# Revit family: CENTUM Festpunkt Typ A mit Massivanschluss XL100, Ø60,3 bis Ø139,7 Gummi_
name_source: partatom
category: HLS-Bauteile
revit_build: Autodesk Revit 2018 (Build: 20190510_1515(x64)
units: mm (PartAtom-declared; Revit-internal decimal feet)

## family parameters
Arbeitsebenenbasiert = Ja
Beim Laden mit Abzugskörper schneiden = Nein
Bemaßung runder Anschluss = Durchmesser verwenden
Gemeinsam genutzt = Ja
Immer vertikal = Nein
Klassifizierung = Keine
Raumberechnungspunkt = Nein
Teiletyp = Normal

## types (5) — shared parameters
Anzahl Rohrschellen = 2
Aufbaumaß = 69 mm
Breite Material Rohrschelle = 50 mm
Fabrikat = MEFA
Klammergröße = 2
Kurztext1 = Festpunkt Typ A
Länge Druckstück = 116 mm
Material Druckstücke = Stahl
Materialname Druckstücke = S235JR
Mengeneinheit = St
Oberfläche Druckstücke = blank
Oberfläche Träger + Schellen = galvanisch verzinkt
Rohrschellentyp = Titan HD
Schalldämmeinlage = Gummi TPE/EPDM
Stärke Material Rohrschelle = 5 mm
Vorgabe-Ansicht = 1219 mm
max. Axiale Reaktionskraft = 20 kN
max. Temperaturbeständigkeit = 100 °C
vpe = 1
zero-valued in all types: max. Höhe, max. Rohraußendurchmesser, min. Rohraußendurchmesser

## per-type parameters (varying)
| type | Artikelnummer | Breite | Breite Profilstahl | EAN | Festpunkt | Gewicht | Gewicht pro Bauteil | Höhe Profilstahl | Kurztext2 | Länge Profilstahl | Profilstahltyp | Rohraußendurchmesser |
| CENTUM Festpunkt Typ A, Ø60,3 mm m. XL100 Massivanshluss, Gummi | 9993633 | 148 mm  [stored 0.485564 ft] | 65 mm | 4250928454188 | Festpunkt Typ A m.XL100 Massivanschluss Ø60 bis 114_1 : CENTUM Festpunkt Typ A, Ø 60,3, m. XL100 Massivanschluss, Gummi | 6.12 kg | 6.12 kg | 42 mm | 60,3 mm Gummi | 200 mm  [stored 0.656168 ft] | U65 | 60 mm  [stored 0.19685 ft] |
| CENTUM Festpunkt Typ A, Ø76,1 mm m. XL100 Massivanshluss, Gummi | 9993732 | 166 mm  [stored 0.544619 ft] | 65 mm | 4250928454218 | Festpunkt Typ A m.XL100 Massivanschluss Ø60 bis 114_1 : CENTUM Festpunkt Typ A, Ø 76,1, m. XL100 Massivanschluss, Gummi | 6.36 kg | 6.36 kg | 42 mm | 76,1 mm Gummi | 200 mm  [stored 0.656168 ft] | U65 | 76 mm  [stored 0.249344 ft] |
| CENTUM Festpunkt Typ A, Ø88,9 mm m. XL100 Massivanshluss, Gummi | 9994027 | 179 mm  [stored 0.58727 ft] | 65 mm | 4250928454232 | Festpunkt Typ A m.XL100 Massivanschluss Ø60 bis 114_1 : CENTUM Festpunkt Typ A, Ø 88,9, m. XL100 Massivanschluss, Gummi | 6.55 kg | 6.55 kg | 42 mm | 88,9 mm Gummi | 0 mm  [stored 0 ft] | U65 | 89 mm |
| CENTUM Festpunkt Typ A, Ø114,3 mm m. XL100 Massivanshluss, Gummi | 9993256 | 205 mm  [stored 0.672572 ft] | 65 mm | 4250928454195 | Festpunkt Typ A m.XL100 Massivanschluss Ø60 bis 114_1 : CENTUM Festpunkt Typ A, Ø114,3, m. XL100 Massivanschluss, Gummi | 6.93 kg | 6.93 kg | 42 mm | 114,3 mm Gummi | 200 mm  [stored 0.656168 ft] | U65 | 114 mm  [stored 0.374016 ft] |
| CENTUM Festpunkt Typ A, Ø139,7 mm m. XL100 Massivanshluss, Gummi | 9993733 | 231 mm  [stored 0.757874 ft] | 80 mm | 4250928454201 | Festpunkt Typ A m.XL100 Massivanschluss Ø139,7_1 : CENTUM Festpunkt Typ A, Ø139,7, m. XL100 Massivanschluss, Gummi | 7.69 kg | 7.69 kg | 45 mm | 139,7 mm Gummi | 200 mm  [stored 0.656168 ft] | U80 | 140 mm |

note: [stored X ft] marks values corroborated as IEEE doubles in the binary element streams (Revit-internal decimal feet)

## geometry (parser evidence)
native form markers: Sweep x17
no freeform markers — native parametric forms only
